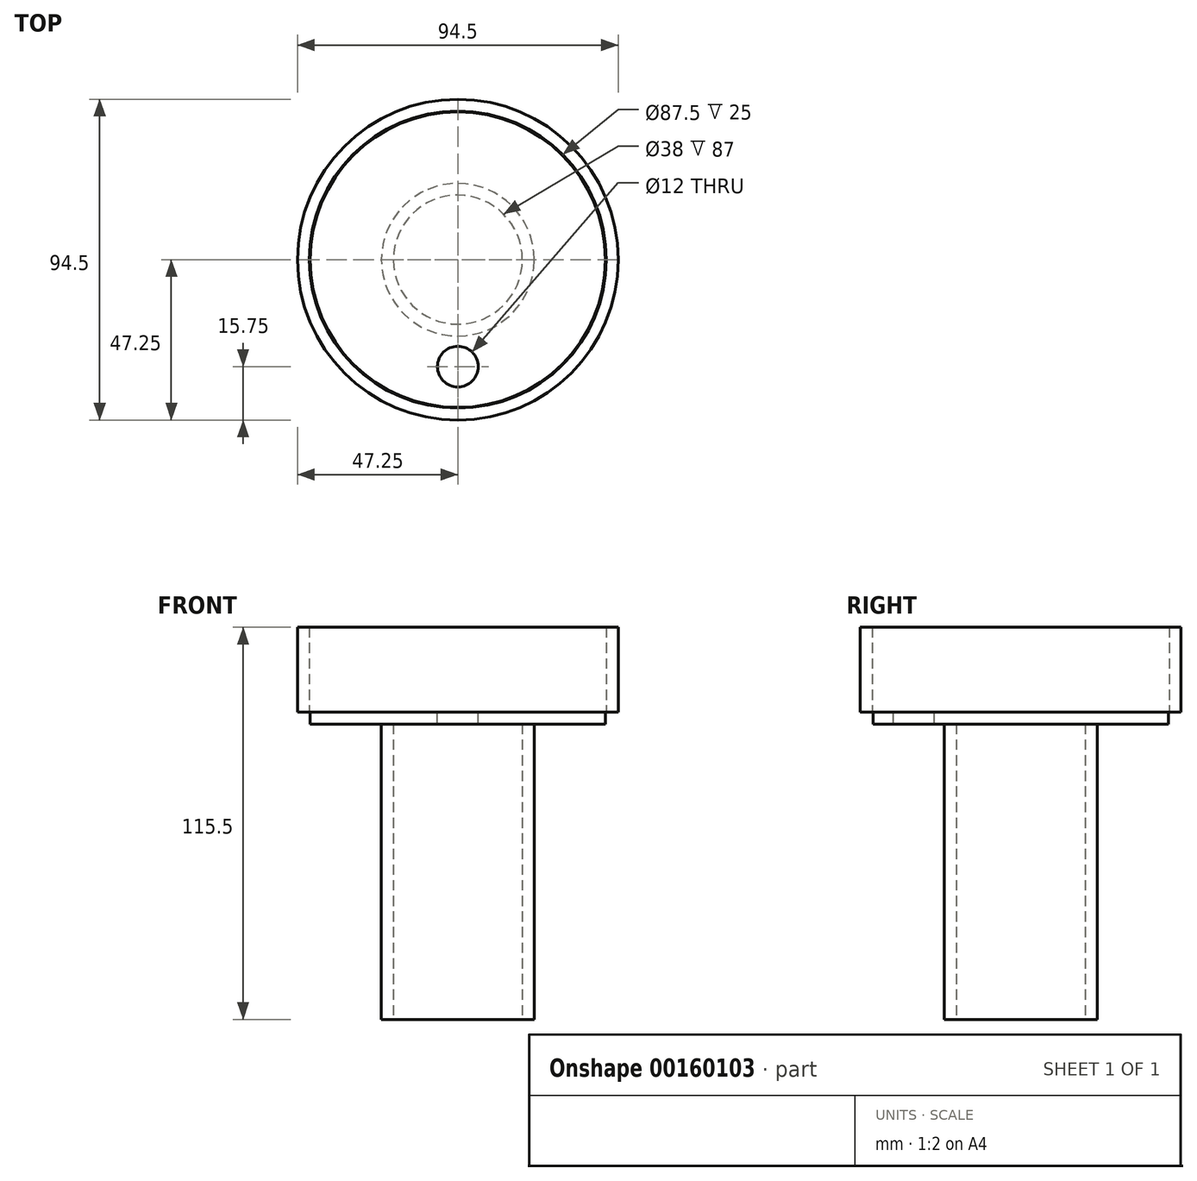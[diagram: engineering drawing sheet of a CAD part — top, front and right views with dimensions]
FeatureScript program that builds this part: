
annotation { "Feature Type Name" : "Feature", "Feature Type Description" : "" }
export const myFeature = defineFeature(function(context is Context, id is Id, definition is map)
    precondition{}
    {
        {
            var Q0;
            Q0=qCreatedBy(makeId("Top.planeOp"),FACE);
            var sketch = newSketch(context, id + "F0", { "sketchPlane" : qUnion([Q0])});
            skCircle(sketch, "E0", {"center": v(0, 0) * mm, "radius": 19 * mm});
            skCircle(sketch, "E1", {"center": v(0, 0) * mm, "radius": 22.5 * mm});
            skSolve(sketch);
        }
        {
            var Q0;
            Q0 = qSketchRegion(id + "F0", true);
            extrude(context, id + "F1", {"entities" : qUnion([Q0]), "depth" : 87 * mm});
        }
        {
            var Q0;
            Q0=makeQuery(id+"F1.opExtrude","CAP_FACE",FACE,{"disambiguationData":[OSD([sQuery(id+"F0.wireOp",EDGE,"E0"),sQuery(id+"F0.wireOp",EDGE,"E1")])],"isStart":false});
            var sketch = newSketch(context, id + "F2", { "sketchPlane" : qUnion([Q0])});
            skCircle(sketch, "E2", {"center": v(0, 0) * mm, "radius": 43.5 * mm});
            skSolve(sketch);
        }
        {
            var Q0;
            Q0 = qSketchRegion(id + "F2", true);
            extrude(context, id + "F3", {"entities" : qUnion([Q0]), "operationType" : NewBodyOperationType.ADD, "depth" : 3.5 * mm});
        }
        {
            var Q0;
            Q0=makeQuery(id+"F3.opExtrude","CAP_FACE",FACE,{"disambiguationData":[OSD([sQuery(id+"F2.wireOp",EDGE,"E2")])],"isStart":false});
            var sketch = newSketch(context, id + "F4", { "sketchPlane" : qUnion([Q0])});
            skCircle(sketch, "E3", {"center": v(0, -31.5) * mm, "radius": 6 * mm});
            skSolve(sketch);
        }
        {
            var Q0;
            Q0 = qSketchRegion(id + "F4", true);
            extrude(context, id + "F5", {"entities" : qUnion([Q0]), "operationType" : NewBodyOperationType.REMOVE, "endBound" : BoundingType.THROUGH_ALL, "oppositeDirection" : true, "depth" : 25 * mm});
        }
        {
            var Q0;
            Q0=makeQuery(id+"F3.opExtrude","CAP_FACE",FACE,{"disambiguationData":[OSD([sQuery(id+"F2.wireOp",EDGE,"E2")])],"isStart":false});
            var sketch = newSketch(context, id + "F6", { "sketchPlane" : qUnion([Q0])});
            skCircle(sketch, "E4", {"center": v(0, 0) * mm, "radius": 43.75 * mm});
            skCircle(sketch, "E5", {"center": v(0, 0) * mm, "radius": 47.25 * mm});
            skSolve(sketch);
        }
        {
            var Q0;
            Q0 = qSketchRegion(id + "F6", true);
            extrude(context, id + "F7", {"entities" : qUnion([Q0]), "depth" : 25 * mm});
        }
    });
